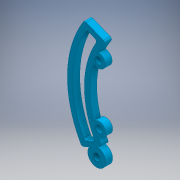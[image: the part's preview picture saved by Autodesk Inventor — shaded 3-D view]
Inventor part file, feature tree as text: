
AUTODESK INVENTOR PART (.ipt)
format: ipt  version: 2017 (Build 210142000, 142)  size: 181,248 bytes
history: native  units: mm
features: extrude x1, fillet x1, sketch x1
ambient origin geometry x8: Origin, YZ Plane, XZ Plane, XY Plane, X Axis, Y Axis, Z Axis, Center Point
bodies: Solid1 (feature_tree)
feature tree (3):
  extrude  "Extrusion1"  Depth=3.0mm
  fillet  "Fillet1"  Radius=3.0mm
  sketch  "Sketch1"  dims[d29=4.0mm d30=3.0mm d31=3.0mm d32=46.25mm d33=43.75mm d34=38.75mm d35=36.25mm d36=36.25mm d37=0.133278mm d38=7.898071mm d39=0.133278mm d40=0.38822mm d41=2.5mm d42=2.107114mm d43=43.168833mm d44=44.35139mm d45=2.060477mm d46=2.043238mm d47=39.493421mm d48=29.517327mm d49=9.276749mm d50=1.620822mm d51=33.414908mm d52=5.795912mm d53=4.299815mm d54=26.089007mm d55=3.0mm d56=0.0mm d57=1.0mm]
